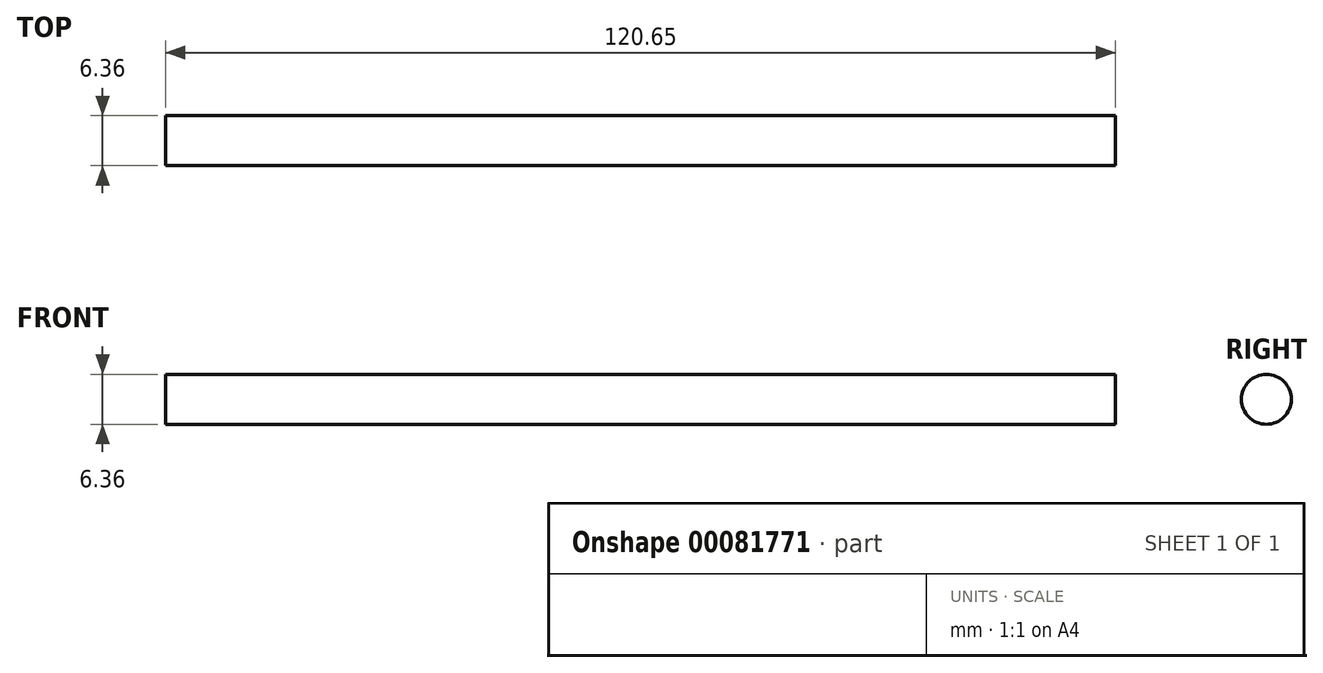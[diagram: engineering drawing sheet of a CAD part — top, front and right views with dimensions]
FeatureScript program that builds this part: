
annotation { "Feature Type Name" : "Feature", "Feature Type Description" : "" }
export const myFeature = defineFeature(function(context is Context, id is Id, definition is map)
    precondition{}
    {
        {
            var Q0;
            Q0=qCreatedBy(makeId("Right.planeOp"),FACE);
            var sketch = newSketch(context, id + "F0", { "sketchPlane" : qUnion([Q0])});
            skCircle(sketch, "E0", {"center": v(0, 0) * mm, "radius": 3.18 * mm});
            skSolve(sketch);
        }
        {
            var Q0;
            Q0 = qSketchRegion(id + "F0", true);
            extrude(context, id + "F1", {"entities" : qUnion([Q0]), "depth" : 120.65 * mm});
        }
    });
